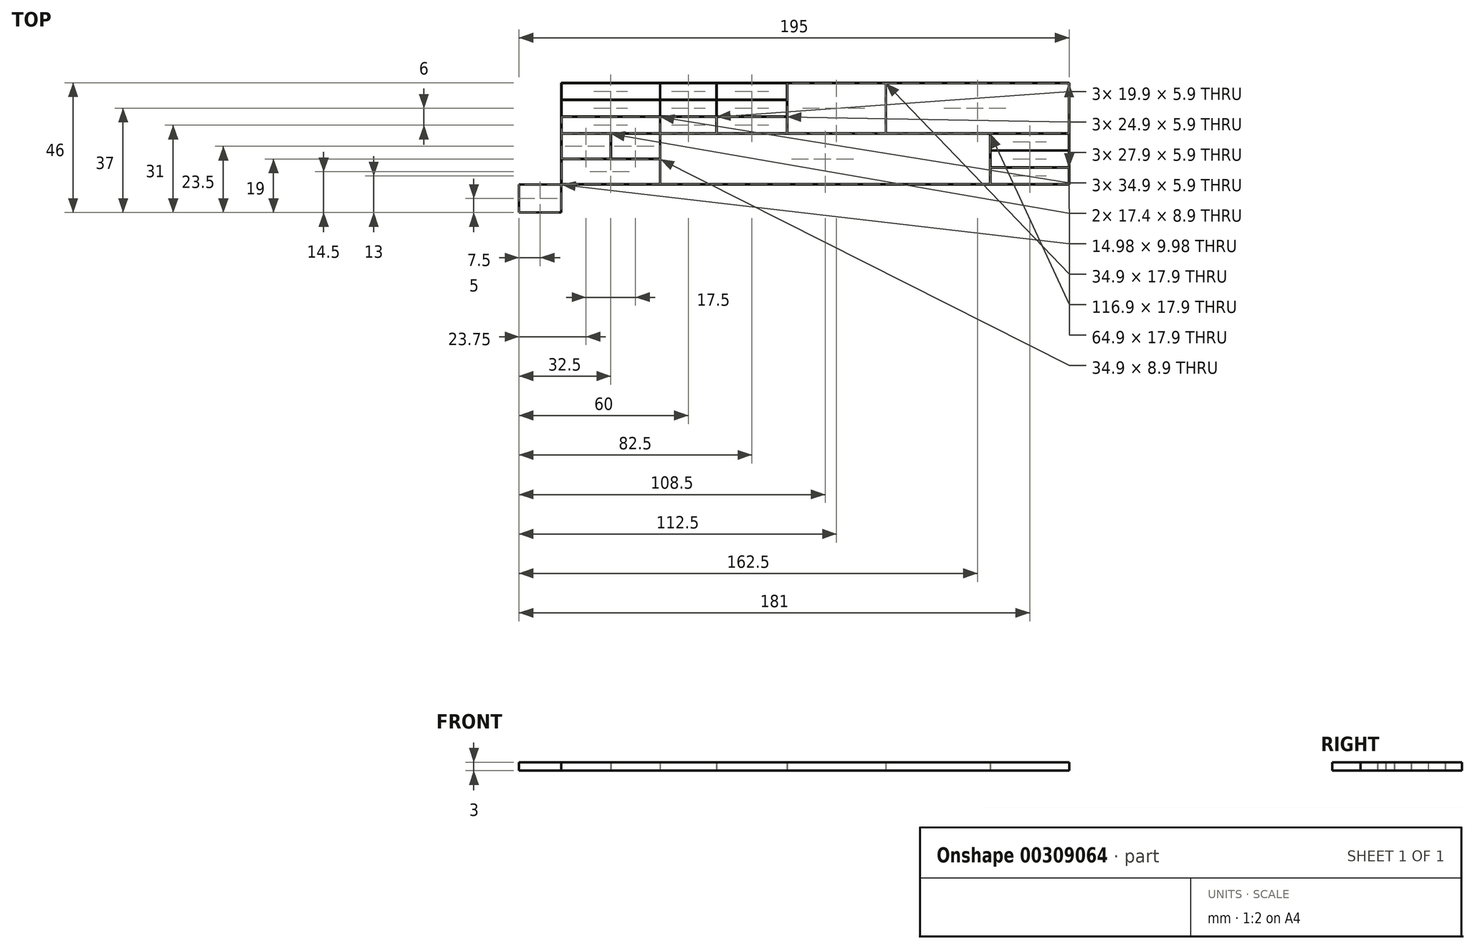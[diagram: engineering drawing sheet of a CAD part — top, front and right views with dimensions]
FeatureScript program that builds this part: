
annotation { "Feature Type Name" : "Feature", "Feature Type Description" : "" }
export const myFeature = defineFeature(function(context is Context, id is Id, definition is map)
    precondition{}
    {
        {
            var Q0;
            Q0=qCreatedBy(makeId("Top.planeOp"),FACE);
            var sketch = newSketch(context, id + "F0", { "sketchPlane" : qUnion([Q0])});
            skLineSegment(sketch, "E0.bottom", {"start": v(0, 0) * mm, "end": v(210, 0) * mm, "construction": true});
            skLineSegment(sketch, "E0.top", {"start": v(0, 290.7) * mm, "end": v(210, 290.7) * mm, "construction": true});
            skLineSegment(sketch, "E0.left", {"start": v(0, 0) * mm, "end": v(0, 290.7) * mm, "construction": true});
            skLineSegment(sketch, "E0.right", {"start": v(210, 0) * mm, "end": v(210, 290.7) * mm, "construction": true});
            skLineSegment(sketch, "E1.0", {"start": v(15, 275.7) * mm, "end": v(195, 275.7) * mm, "construction": true});
            skLineSegment(sketch, "E1.1", {"start": v(15, 15) * mm, "end": v(15, 275.7) * mm, "construction": true});
            skLineSegment(sketch, "E1.2", {"start": v(15, 15) * mm, "end": v(195, 15) * mm, "construction": true});
            skLineSegment(sketch, "E1.3", {"start": v(195, 15) * mm, "end": v(195, 275.7) * mm, "construction": true});
            skLineSegment(sketch, "E2", {"start": v(15, 51) * mm, "end": v(195, 51) * mm, "construction": true});
            skLineSegment(sketch, "E3.bottom", {"start": v(15, 15) * mm, "end": v(0, 15) * mm});
            skLineSegment(sketch, "E3.top", {"start": v(15, 0) * mm, "end": v(0, 0) * mm});
            skLineSegment(sketch, "E3.left", {"start": v(15, 15) * mm, "end": v(15, 0) * mm, "construction": true});
            skLineSegment(sketch, "E3.right", {"start": v(0, 15) * mm, "end": v(0, 0) * mm});
            skPoint(sketch, "E4.middle", {"position": v(7.5, 7.5) * mm});
            skPoint(sketch, "E4.middle.positionSnap0", {"position": v(7.5, 15) * mm});
            skPoint(sketch, "E4.middle.positionSnap1", {"position": v(0, 7.5) * mm});
            skPoint(sketch, "E4.centerSnap0", {"position": v(7.5, 15) * mm});
            skPoint(sketch, "E4.centerSnap1", {"position": v(0, 7.5) * mm});
            skLineSegment(sketch, "E5.top", {"start": v(15, 5) * mm, "end": v(0, 5) * mm});
            skLineSegment(sketch, "E5.left", {"start": v(15, 15) * mm, "end": v(15, 5) * mm});
            skLineSegment(sketch, "E5.right", {"start": v(0, 15) * mm, "end": v(0, 5) * mm});
            skLineSegment(sketch, "E6.bottom", {"start": v(0.01, 15) * mm, "end": v(15, 15) * mm});
            skLineSegment(sketch, "E6.top", {"start": v(0.01, 5.01) * mm, "end": v(15, 5.01) * mm});
            skLineSegment(sketch, "E6.left", {"start": v(0.01, 15) * mm, "end": v(0.01, 5.01) * mm});
            skLineSegment(sketch, "E6.right", {"start": v(15, 15) * mm, "end": v(15, 5.01) * mm});
            skSolve(sketch);
        }
        {
            var Q0;
            Q0=qCreatedBy(makeId("Top.planeOp"),FACE);
            var sketch = newSketch(context, id + "F1", { "sketchPlane" : qUnion([Q0])});
            skLineSegment(sketch, "E7.bottom", {"start": v(15, 51) * mm, "end": v(195, 51) * mm});
            skLineSegment(sketch, "E7.top", {"start": v(15, 15) * mm, "end": v(195, 15) * mm});
            skLineSegment(sketch, "E7.left", {"start": v(15, 51) * mm, "end": v(15, 15) * mm});
            skLineSegment(sketch, "E7.right", {"start": v(195, 51) * mm, "end": v(195, 15) * mm});
            skLineSegment(sketch, "E8.bottom", {"start": v(15, 51) * mm, "end": v(50, 51) * mm});
            skLineSegment(sketch, "E8.top", {"start": v(15, 45) * mm, "end": v(50, 45) * mm});
            skLineSegment(sketch, "E8.left", {"start": v(15, 51) * mm, "end": v(15, 45) * mm});
            skLineSegment(sketch, "E8.right", {"start": v(50, 51) * mm, "end": v(50, 45) * mm});
            skLineSegment(sketch, "E9.bottom", {"start": v(50, 45) * mm, "end": v(70, 45) * mm});
            skLineSegment(sketch, "E9.top", {"start": v(50, 51) * mm, "end": v(70, 51) * mm});
            skLineSegment(sketch, "E9.left", {"start": v(50, 45) * mm, "end": v(50, 51) * mm});
            skLineSegment(sketch, "E9.right", {"start": v(70, 45) * mm, "end": v(70, 51) * mm});
            skLineSegment(sketch, "E10.top", {"start": v(15, 39) * mm, "end": v(50, 39) * mm});
            skLineSegment(sketch, "E10.left", {"start": v(15, 45) * mm, "end": v(15, 39) * mm});
            skLineSegment(sketch, "E10.right", {"start": v(50, 45) * mm, "end": v(50, 39) * mm});
            skLineSegment(sketch, "E11.bottom", {"start": v(50, 39) * mm, "end": v(70, 39) * mm});
            skLineSegment(sketch, "E11.left", {"start": v(50, 39) * mm, "end": v(50, 45) * mm});
            skLineSegment(sketch, "E11.right", {"start": v(70, 39) * mm, "end": v(70, 45) * mm});
            skLineSegment(sketch, "E12.top", {"start": v(15, 33) * mm, "end": v(50, 33) * mm});
            skLineSegment(sketch, "E12.left", {"start": v(15, 39) * mm, "end": v(15, 33) * mm});
            skLineSegment(sketch, "E12.right", {"start": v(50, 39) * mm, "end": v(50, 33) * mm});
            skLineSegment(sketch, "E13.bottom", {"start": v(50, 33) * mm, "end": v(70, 33) * mm});
            skLineSegment(sketch, "E13.left", {"start": v(50, 33) * mm, "end": v(50, 39) * mm});
            skLineSegment(sketch, "E13.right", {"start": v(70, 33) * mm, "end": v(70, 39) * mm});
            skLineSegment(sketch, "E14.bottom", {"start": v(70, 45) * mm, "end": v(95, 45) * mm});
            skLineSegment(sketch, "E14.top", {"start": v(70, 51) * mm, "end": v(95, 51) * mm});
            skLineSegment(sketch, "E14.right", {"start": v(95, 45) * mm, "end": v(95, 51) * mm});
            skLineSegment(sketch, "E15.bottom", {"start": v(70, 39) * mm, "end": v(95, 39) * mm});
            skLineSegment(sketch, "E15.right", {"start": v(95, 39) * mm, "end": v(95, 45) * mm});
            skLineSegment(sketch, "E16.bottom", {"start": v(70, 33) * mm, "end": v(95, 33) * mm});
            skLineSegment(sketch, "E16.right", {"start": v(95, 33) * mm, "end": v(95, 39) * mm});
            skPoint(sketch, "E17.oppositeSnap0", {"position": v(32.5, 33) * mm});
            skLineSegment(sketch, "E17.bottom", {"start": v(15, 33) * mm, "end": v(32.5, 33) * mm});
            skLineSegment(sketch, "E17.top", {"start": v(15, 24) * mm, "end": v(32.5, 24) * mm});
            skLineSegment(sketch, "E17.left", {"start": v(15, 33) * mm, "end": v(15, 24) * mm});
            skLineSegment(sketch, "E17.right", {"start": v(32.5, 33) * mm, "end": v(32.5, 24) * mm});
            skLineSegment(sketch, "E18.bottom", {"start": v(32.5, 24) * mm, "end": v(50, 24) * mm});
            skLineSegment(sketch, "E18.top", {"start": v(32.5, 33) * mm, "end": v(50, 33) * mm});
            skLineSegment(sketch, "E18.left", {"start": v(32.5, 24) * mm, "end": v(32.5, 33) * mm});
            skLineSegment(sketch, "E18.right", {"start": v(50, 24) * mm, "end": v(50, 33) * mm});
            skLineSegment(sketch, "E19.bottom", {"start": v(15, 24) * mm, "end": v(50, 24) * mm});
            skLineSegment(sketch, "E19.top", {"start": v(15, 15) * mm, "end": v(50, 15) * mm});
            skLineSegment(sketch, "E19.left", {"start": v(15, 24) * mm, "end": v(15, 15) * mm});
            skLineSegment(sketch, "E19.right", {"start": v(50, 24) * mm, "end": v(50, 15) * mm});
            skPoint(sketch, "E20.oppositeSnap0", {"position": v(41.25, 33) * mm});
            skLineSegment(sketch, "E20.bottom", {"start": v(50, 15) * mm, "end": v(167, 15) * mm});
            skLineSegment(sketch, "E20.top", {"start": v(50, 33) * mm, "end": v(167, 33) * mm});
            skLineSegment(sketch, "E20.left", {"start": v(50, 15) * mm, "end": v(50, 33) * mm});
            skLineSegment(sketch, "E20.right", {"start": v(167, 15) * mm, "end": v(167, 33) * mm});
            skLineSegment(sketch, "E21.bottom", {"start": v(167, 33) * mm, "end": v(195, 33) * mm});
            skLineSegment(sketch, "E21.top", {"start": v(167, 27) * mm, "end": v(195, 27) * mm});
            skLineSegment(sketch, "E21.left", {"start": v(167, 33) * mm, "end": v(167, 27) * mm});
            skLineSegment(sketch, "E21.right", {"start": v(195, 33) * mm, "end": v(195, 27) * mm});
            skLineSegment(sketch, "E22.top", {"start": v(167, 21) * mm, "end": v(195, 21) * mm});
            skLineSegment(sketch, "E22.left", {"start": v(167, 27) * mm, "end": v(167, 21) * mm});
            skLineSegment(sketch, "E22.right", {"start": v(195, 27) * mm, "end": v(195, 21) * mm});
            skLineSegment(sketch, "E23.top", {"start": v(167, 15) * mm, "end": v(195, 15) * mm});
            skLineSegment(sketch, "E23.left", {"start": v(167, 21) * mm, "end": v(167, 15) * mm});
            skLineSegment(sketch, "E23.right", {"start": v(195, 21) * mm, "end": v(195, 15) * mm});
            skLineSegment(sketch, "E24.bottom", {"start": v(195, 33) * mm, "end": v(130, 33) * mm});
            skLineSegment(sketch, "E24.top", {"start": v(195, 51) * mm, "end": v(130, 51) * mm});
            skLineSegment(sketch, "E24.left", {"start": v(195, 33) * mm, "end": v(195, 51) * mm});
            skLineSegment(sketch, "E24.right", {"start": v(130, 33) * mm, "end": v(130, 51) * mm});
            skLineSegment(sketch, "E25.bottom", {"start": v(130, 33) * mm, "end": v(95, 33) * mm});
            skLineSegment(sketch, "E25.top", {"start": v(130, 51) * mm, "end": v(95, 51) * mm});
            skLineSegment(sketch, "E25.right", {"start": v(95, 33) * mm, "end": v(95, 51) * mm});
            skPoint(sketch, "E26", {"position": v(32.5, 51) * mm});
            skPoint(sketch, "E27", {"position": v(15, 48) * mm});
            skPoint(sketch, "E28", {"position": v(15, 42) * mm});
            skPoint(sketch, "E29", {"position": v(15, 36) * mm});
            skSolve(sketch);
        }
        {
            var Q0;
            Q0=qCreatedBy(makeId("Top.planeOp"),FACE);
            var sketch = newSketch(context, id + "F2", { "sketchPlane" : qUnion([Q0])});
            skPoint(sketch, "E30", {"position": v(15, 48) * mm});
            skPoint(sketch, "E31", {"position": v(15, 42) * mm});
            skPoint(sketch, "E32", {"position": v(15, 36) * mm});
            skPoint(sketch, "E33", {"position": v(15, 19.5) * mm});
            skPoint(sketch, "E34", {"position": v(32.5, 51) * mm});
            skPoint(sketch, "E35", {"position": v(60, 51) * mm});
            skPoint(sketch, "E36", {"position": v(112.5, 51) * mm});
            skPoint(sketch, "E37", {"position": v(82.5, 45) * mm});
            skPoint(sketch, "E38", {"position": v(167, 24) * mm});
            skPoint(sketch, "E39", {"position": v(32.5, 15) * mm});
            skPoint(sketch, "E40", {"position": v(32.5, 28.5) * mm});
            skPoint(sketch, "E41", {"position": v(167, 18) * mm});
            skPoint(sketch, "E42", {"position": v(181, 15) * mm});
            skLineSegment(sketch, "E43.bottom", {"start": v(49.95, 50.95) * mm, "end": v(15.05, 50.95) * mm});
            skLineSegment(sketch, "E43.top", {"start": v(49.95, 45.05) * mm, "end": v(15.05, 45.05) * mm});
            skLineSegment(sketch, "E43.left", {"start": v(49.95, 50.95) * mm, "end": v(49.95, 45.05) * mm});
            skLineSegment(sketch, "E43.right", {"start": v(15.05, 50.95) * mm, "end": v(15.05, 45.05) * mm});
            skPoint(sketch, "E43.middle", {"position": v(32.5, 48) * mm});
            skLineSegment(sketch, "E44.bottom", {"start": v(49.95, 44.95) * mm, "end": v(15.05, 44.95) * mm});
            skLineSegment(sketch, "E44.top", {"start": v(49.95, 39.05) * mm, "end": v(15.05, 39.05) * mm});
            skLineSegment(sketch, "E44.left", {"start": v(49.95, 44.95) * mm, "end": v(49.95, 39.05) * mm});
            skLineSegment(sketch, "E44.right", {"start": v(15.05, 44.95) * mm, "end": v(15.05, 39.05) * mm});
            skPoint(sketch, "E44.middle", {"position": v(32.5, 42) * mm});
            skPoint(sketch, "E44.middle.positionSnap0", {"position": v(32.5, 45.05) * mm});
            skPoint(sketch, "E44.centerSnap0", {"position": v(32.5, 45.05) * mm});
            skLineSegment(sketch, "E45.bottom", {"start": v(49.95, 38.95) * mm, "end": v(15.05, 38.95) * mm});
            skLineSegment(sketch, "E45.top", {"start": v(49.95, 33.05) * mm, "end": v(15.05, 33.05) * mm});
            skLineSegment(sketch, "E45.left", {"start": v(49.95, 38.95) * mm, "end": v(49.95, 33.05) * mm});
            skLineSegment(sketch, "E45.right", {"start": v(15.05, 38.95) * mm, "end": v(15.05, 33.05) * mm});
            skPoint(sketch, "E45.middle", {"position": v(32.5, 36) * mm});
            skLineSegment(sketch, "E46.bottom", {"start": v(49.95, 23.95) * mm, "end": v(15.05, 23.95) * mm});
            skLineSegment(sketch, "E46.top", {"start": v(49.95, 15.05) * mm, "end": v(15.05, 15.05) * mm});
            skLineSegment(sketch, "E46.left", {"start": v(49.95, 23.95) * mm, "end": v(49.95, 15.05) * mm});
            skLineSegment(sketch, "E46.right", {"start": v(15.05, 23.95) * mm, "end": v(15.05, 15.05) * mm});
            skPoint(sketch, "E46.middle", {"position": v(32.5, 19.5) * mm});
            skPoint(sketch, "E47", {"position": v(23.75, 33) * mm});
            skLineSegment(sketch, "E48.bottom", {"start": v(32.45, 32.95) * mm, "end": v(15.05, 32.95) * mm});
            skLineSegment(sketch, "E48.top", {"start": v(32.45, 24.05) * mm, "end": v(15.05, 24.05) * mm});
            skLineSegment(sketch, "E48.left", {"start": v(32.45, 32.95) * mm, "end": v(32.45, 24.05) * mm});
            skLineSegment(sketch, "E48.right", {"start": v(15.05, 32.95) * mm, "end": v(15.05, 24.05) * mm});
            skPoint(sketch, "E48.middle", {"position": v(23.75, 28.5) * mm});
            skPoint(sketch, "E49", {"position": v(41.25, 33) * mm});
            skLineSegment(sketch, "E50.bottom", {"start": v(32.55, 32.95) * mm, "end": v(49.95, 32.95) * mm});
            skLineSegment(sketch, "E50.top", {"start": v(32.55, 24.05) * mm, "end": v(49.95, 24.05) * mm});
            skLineSegment(sketch, "E50.left", {"start": v(32.55, 32.95) * mm, "end": v(32.55, 24.05) * mm});
            skLineSegment(sketch, "E50.right", {"start": v(49.95, 32.95) * mm, "end": v(49.95, 24.05) * mm});
            skPoint(sketch, "E50.middle", {"position": v(41.25, 28.5) * mm});
            skLineSegment(sketch, "E51.bottom", {"start": v(69.95, 50.95) * mm, "end": v(50.05, 50.95) * mm});
            skLineSegment(sketch, "E51.top", {"start": v(69.95, 45.05) * mm, "end": v(50.05, 45.05) * mm});
            skLineSegment(sketch, "E51.left", {"start": v(69.95, 50.95) * mm, "end": v(69.95, 45.05) * mm});
            skLineSegment(sketch, "E51.right", {"start": v(50.05, 50.95) * mm, "end": v(50.05, 45.05) * mm});
            skPoint(sketch, "E51.middle", {"position": v(60, 48) * mm});
            skLineSegment(sketch, "E52.bottom", {"start": v(50.05, 44.95) * mm, "end": v(69.95, 44.95) * mm});
            skLineSegment(sketch, "E52.top", {"start": v(50.05, 39.05) * mm, "end": v(69.95, 39.05) * mm});
            skLineSegment(sketch, "E52.left", {"start": v(50.05, 44.95) * mm, "end": v(50.05, 39.05) * mm});
            skLineSegment(sketch, "E52.right", {"start": v(69.95, 44.95) * mm, "end": v(69.95, 39.05) * mm});
            skPoint(sketch, "E52.middle", {"position": v(60, 42) * mm});
            skLineSegment(sketch, "E53.bottom", {"start": v(50.05, 38.95) * mm, "end": v(69.95, 38.95) * mm});
            skLineSegment(sketch, "E53.top", {"start": v(50.05, 33.05) * mm, "end": v(69.95, 33.05) * mm});
            skLineSegment(sketch, "E53.left", {"start": v(50.05, 38.95) * mm, "end": v(50.05, 33.05) * mm});
            skLineSegment(sketch, "E53.right", {"start": v(69.95, 38.95) * mm, "end": v(69.95, 33.05) * mm});
            skPoint(sketch, "E53.middle", {"position": v(60, 36) * mm});
            skPoint(sketch, "E53.middle.positionSnap0", {"position": v(49.95, 36) * mm});
            skPoint(sketch, "E53.middle.positionSnap1", {"position": v(60, 39.05) * mm});
            skPoint(sketch, "E53.centerSnap0", {"position": v(49.95, 36) * mm});
            skPoint(sketch, "E53.centerSnap1", {"position": v(60, 39.05) * mm});
            skLineSegment(sketch, "E54.bottom", {"start": v(70.05, 45.05) * mm, "end": v(94.95, 45.05) * mm});
            skLineSegment(sketch, "E54.top", {"start": v(70.05, 50.95) * mm, "end": v(94.95, 50.95) * mm});
            skLineSegment(sketch, "E54.left", {"start": v(70.05, 45.05) * mm, "end": v(70.05, 50.95) * mm});
            skLineSegment(sketch, "E54.right", {"start": v(94.95, 45.05) * mm, "end": v(94.95, 50.95) * mm});
            skPoint(sketch, "E54.middle", {"position": v(82.5, 48) * mm});
            skPoint(sketch, "E54.middle.positionSnap0", {"position": v(69.95, 48) * mm});
            skPoint(sketch, "E54.centerSnap0", {"position": v(69.95, 48) * mm});
            skLineSegment(sketch, "E55.bottom", {"start": v(70.05, 44.95) * mm, "end": v(94.95, 44.95) * mm});
            skLineSegment(sketch, "E55.top", {"start": v(70.05, 39.05) * mm, "end": v(94.95, 39.05) * mm});
            skLineSegment(sketch, "E55.left", {"start": v(70.05, 44.95) * mm, "end": v(70.05, 39.05) * mm});
            skLineSegment(sketch, "E55.right", {"start": v(94.95, 44.95) * mm, "end": v(94.95, 39.05) * mm});
            skPoint(sketch, "E55.middle", {"position": v(82.5, 42) * mm});
            skLineSegment(sketch, "E56.bottom", {"start": v(70.05, 38.95) * mm, "end": v(94.95, 38.95) * mm});
            skLineSegment(sketch, "E56.top", {"start": v(70.05, 33.05) * mm, "end": v(94.95, 33.05) * mm});
            skLineSegment(sketch, "E56.left", {"start": v(70.05, 38.95) * mm, "end": v(70.05, 33.05) * mm});
            skLineSegment(sketch, "E56.right", {"start": v(94.95, 38.95) * mm, "end": v(94.95, 33.05) * mm});
            skPoint(sketch, "E56.middle", {"position": v(82.5, 36) * mm});
            skLineSegment(sketch, "E57.bottom", {"start": v(95.05, 50.95) * mm, "end": v(129.95, 50.95) * mm});
            skLineSegment(sketch, "E57.top", {"start": v(95.05, 33.05) * mm, "end": v(129.95, 33.05) * mm});
            skLineSegment(sketch, "E57.left", {"start": v(95.05, 50.95) * mm, "end": v(95.05, 33.05) * mm});
            skLineSegment(sketch, "E57.right", {"start": v(129.95, 50.95) * mm, "end": v(129.95, 33.05) * mm});
            skPoint(sketch, "E57.middle", {"position": v(112.5, 42) * mm});
            skPoint(sketch, "E57.middle.positionSnap0", {"position": v(94.95, 42) * mm});
            skPoint(sketch, "E57.centerSnap0", {"position": v(94.95, 42) * mm});
            skLineSegment(sketch, "E58.bottom", {"start": v(194.95, 20.95) * mm, "end": v(167.05, 20.95) * mm});
            skLineSegment(sketch, "E58.top", {"start": v(194.95, 15.05) * mm, "end": v(167.05, 15.05) * mm});
            skLineSegment(sketch, "E58.left", {"start": v(194.95, 20.95) * mm, "end": v(194.95, 15.05) * mm});
            skLineSegment(sketch, "E58.right", {"start": v(167.05, 20.95) * mm, "end": v(167.05, 15.05) * mm});
            skPoint(sketch, "E58.middle", {"position": v(181, 18) * mm});
            skLineSegment(sketch, "E59.bottom", {"start": v(167.05, 21.05) * mm, "end": v(194.95, 21.05) * mm});
            skLineSegment(sketch, "E59.top", {"start": v(167.05, 26.95) * mm, "end": v(194.95, 26.95) * mm});
            skLineSegment(sketch, "E59.left", {"start": v(167.05, 21.05) * mm, "end": v(167.05, 26.95) * mm});
            skLineSegment(sketch, "E59.right", {"start": v(194.95, 21.05) * mm, "end": v(194.95, 26.95) * mm});
            skPoint(sketch, "E59.middle", {"position": v(181, 24) * mm});
            skPoint(sketch, "E60", {"position": v(105, 15) * mm});
            skLineSegment(sketch, "E61.bottom", {"start": v(194.95, 27.05) * mm, "end": v(167.05, 27.05) * mm});
            skLineSegment(sketch, "E61.top", {"start": v(194.95, 32.95) * mm, "end": v(167.05, 32.95) * mm});
            skLineSegment(sketch, "E61.left", {"start": v(194.95, 27.05) * mm, "end": v(194.95, 32.95) * mm});
            skLineSegment(sketch, "E61.right", {"start": v(167.05, 27.05) * mm, "end": v(167.05, 32.95) * mm});
            skLineSegment(sketch, "E62.bottom", {"start": v(130.05, 33.05) * mm, "end": v(194.95, 33.05) * mm});
            skLineSegment(sketch, "E62.top", {"start": v(130.05, 50.95) * mm, "end": v(194.95, 50.95) * mm});
            skLineSegment(sketch, "E62.left", {"start": v(130.05, 33.05) * mm, "end": v(130.05, 50.95) * mm});
            skLineSegment(sketch, "E62.right", {"start": v(194.95, 33.05) * mm, "end": v(194.95, 50.95) * mm});
            skLineSegment(sketch, "E63.bottom", {"start": v(15, 51) * mm, "end": v(195, 51) * mm});
            skLineSegment(sketch, "E63.top", {"start": v(15, 15) * mm, "end": v(195, 15) * mm});
            skLineSegment(sketch, "E63.left", {"start": v(15, 51) * mm, "end": v(15, 15) * mm});
            skLineSegment(sketch, "E63.right", {"start": v(195, 51) * mm, "end": v(195, 15) * mm});
            skLineSegment(sketch, "E64.bottom", {"start": v(50.05, 32.95) * mm, "end": v(166.95, 32.95) * mm});
            skLineSegment(sketch, "E64.top", {"start": v(50.05, 15.05) * mm, "end": v(166.95, 15.05) * mm});
            skLineSegment(sketch, "E64.left", {"start": v(50.05, 32.95) * mm, "end": v(50.05, 15.05) * mm});
            skLineSegment(sketch, "E64.right", {"start": v(166.95, 32.95) * mm, "end": v(166.95, 15.05) * mm});
            skSolve(sketch);
        }
        {
            var Q0;
            Q0=makeQuery(id+"F2.imprint","IMPRINT",FACE,{"disambiguationData":[TD([[makeQuery(id+"F2.imprint","IMPRINT",EDGE,{"derivedFrom":sQuery(id+"F2.wireOp",EDGE,"E43.bottom")}),-1.0]])]});
            extrude(context, id + "F3", {"entities" : qUnion([Q0]), "depth" : 3 * mm});
        }
        {
            var Q0;
            Q0=makeQuery(id+"F0.imprint","IMPRINT",FACE,{"disambiguationData":[TD([[makeQuery(id+"F0.imprint","IMPRINT",EDGE,{"derivedFrom":sQuery(id+"F0.wireOp",EDGE,"E3.bottom")}),1.0]])]});
            extrude(context, id + "F4", {"entities" : qUnion([Q0]), "depth" : 3 * mm});
        }
    });
